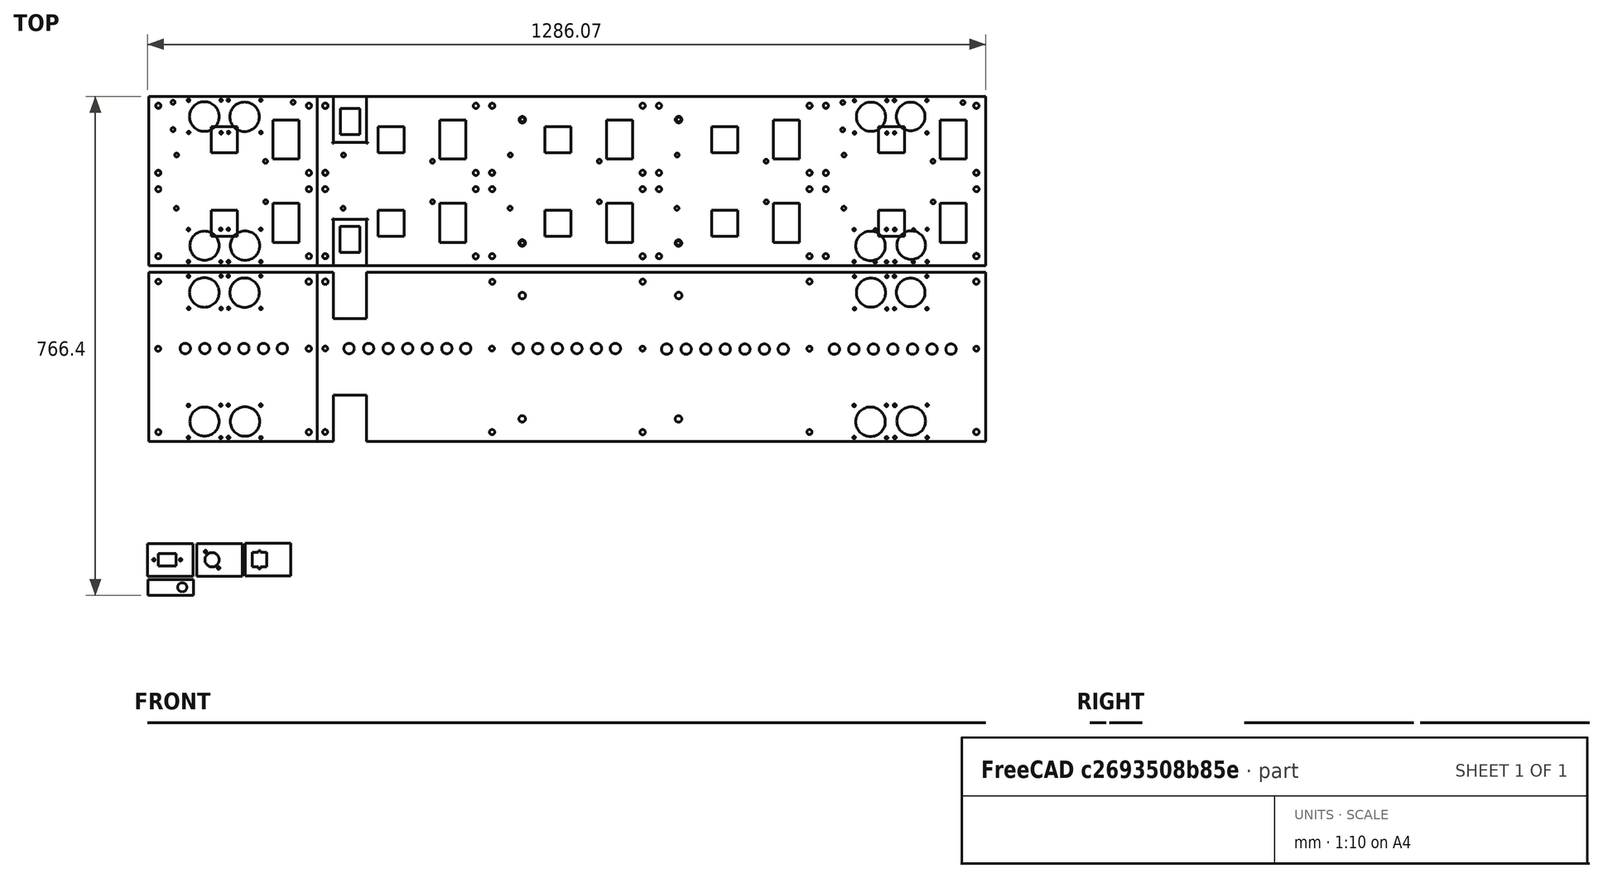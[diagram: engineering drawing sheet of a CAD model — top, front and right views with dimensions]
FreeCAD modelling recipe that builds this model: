
FCSTD DOCUMENT  (FreeCAD 1.0R39319 (Git))
Label: SurfSign-Case-4.2
License: All rights reserved
LicenseURL: https://en.wikipedia.org/wiki/All_rights_reserved
objects: Part::Part2DObjectPython×16, Part::FeaturePython×12, Part::Feature×4, Part::Cut×3, App::DocumentObjectGroup×2
note: 35 computed .brp shape members not serialized (recipe doc carries the construction recipe); baked Part::Feature solids carry a one-line shape summary decoded from their .brp

FEATURE [Part::Part2DObjectPython] Rectangle024  label="SidesLarge"  # Draft 2D object (typed FeaturePython)
  Area = 55782
  ChamferSize = 0
  Columns = 1
  FilletRadius = 0
  Height = 54
  Length = 1033
  MakeFace = true
  Placement = pos=(95.949,-98.4324,0) rot=(0,0,1;0rad)
  Rows = 1
FEATURE [Part::Part2DObjectPython] Rectangle026  label="SidesSmall"  # Draft 2D object (typed FeaturePython)
  Area = 14040
  ChamferSize = 0
  Columns = 1
  FilletRadius = 0
  Height = 54
  Length = 260
  MakeFace = true
  Placement = pos=(93.675,-166.174,0) rot=(0,0,1;0rad)
  Rows = 1
FEATURE [Part::Part2DObjectPython] Rectangle027  # Draft 2D object (typed FeaturePython)
  Area = 1722
  ChamferSize = 0
  Columns = 1
  FilletRadius = 0
  Height = 24.6
  Length = 70
  MakeFace = true
  Placement = pos=(121.424,-273.33,0) rot=(0,0,1;0rad)
  Rows = 1
FEATURE [Part::Part2DObjectPython] Circle024  # Draft 2D object (typed FeaturePython)
  Area = 153.938
  FirstAngle = 0
  LastAngle = 0
  MakeFace = true
  Placement = pos=(173.98,-260.68,0) rot=(0,0,1;0rad)
  Radius = 7
FEATURE [Part::Cut] Cut017  label="PeriphrealSides"
  Base = -> Rectangle027
  Placement = pos=(-22.8217,16.9303,0) rot=(0,0,1;0rad)
  Refine = true
  Tool = -> Circle024
FEATURE [Part::Feature] Subtraction032  label="PeriphrealPower"
  Placement = pos=(-0.595688,35.1452,0) rot=(0,0,1;0rad)
  shape: bbox 70 x 50 x 2e-07 mm, 1 faces, 0 solids (baked)
FEATURE [Part::Part2DObjectPython] Rectangle029  # Draft 2D object (typed FeaturePython)
  Area = 484
  ChamferSize = 0
  Columns = 1
  FilletRadius = 0
  Height = 22
  Length = 22
  MakeFace = true
  Placement = pos=(110.321,-299.863,0) rot=(0,0,1;0rad)
  Rows = 1
FEATURE [Part::Part2DObjectPython] Rectangle028  # Draft 2D object (typed FeaturePython)
  Area = 3500
  ChamferSize = 0
  Columns = 1
  FilletRadius = 0
  Height = 50
  Length = 70
  MakeFace = true
  Placement = pos=(99.2536,-313.899,0) rot=(0,0,1;0rad)
  Rows = 1
FEATURE [Part::Cut] Cut018
  Base = -> Rectangle028
  Refine = true
  Tool = -> Rectangle029
FEATURE [Part::Part2DObjectPython] Rectangle031  # Draft 2D object (typed FeaturePython)
  Area = 84
  ChamferSize = 0
  Columns = 1
  FilletRadius = 0
  Height = 28
  Length = 3
  MakeFace = true
  Placement = pos=(119.9,-302.833,0) rot=(0,0,1;0rad)
  Rows = 1
FEATURE [Part::Cut] Cut019  label="PeriphrealRJ45A"
  Base = -> Cut018
  Placement = pos=(148.325,87.5652,0) rot=(0,0,1;0rad)
  Refine = true
  Tool = -> Rectangle031
FEATURE [Part::Feature] Subtraction033  label="PeriphrealRJ45B"
  Placement = pos=(73.2688,140.581,0) rot=(0,0,1;0rad)
  shape: bbox 70 x 50 x 2e-07 mm, 1 faces, 0 solids (baked)
FEATURE [Part::FeaturePython] Clone  label="Backplate"  # WARN: FeaturePython — macro-defined, semantics opaque (R4)
  AttacherType = Attacher::AttachEngine3D
  Fuse = false
  Placement = pos=(2.11317,-14.857,0) rot=(0,0,1;0rad)
  Scale = (1,1,1)
FEATURE [Part::Part2DObjectPython] Rectangle032  label="SidesLarge001"  # Draft 2D object (typed FeaturePython)
  Area = 55782
  ChamferSize = 0
  Columns = 1
  FilletRadius = 0
  Height = 54
  Length = 1033
  MakeFace = true
  Placement = pos=(95.949,-98.4324,0) rot=(0,0,1;0rad)
  Rows = 1
FEATURE [Part::Feature] Subtraction
  shape: bbox 1284 x 260 x 2e-07 mm, 1 faces, 0 solids (baked)
FEATURE [Part::Part2DObjectPython] Line  # Draft 2D object (typed FeaturePython)
  Area = 0
  ChamferSize = 0
  Closed = false
  End = (358,558.007,0)
  FilletRadius = 0
  Length = 578.437
  MakeFace = true
  Placement = pos=(358,-20.4298,0) rot=(0,0,1;0rad)
  Points = (2) [(0,0,0),(0,578.437,0)]
  Start = (358,-20.4298,0)
  Subdivisions = 0
FEATURE [Part::Part2DObjectPython] Rectangle  # Draft 2D object (typed FeaturePython)
  Area = 8149.48
  ChamferSize = 0
  Columns = 1
  FilletRadius = 0
  Height = 42.278
  Length = 192.759
  MakeFace = true
  Placement = pos=(146.23,98.5195,0) rot=(0,0,1;0rad)
  Rows = 1
FEATURE [Part::Part2DObjectPython] Rectangle033  # Draft 2D object (typed FeaturePython)
  Area = 12120.2
  ChamferSize = 0
  Columns = 1
  FilletRadius = 0
  Height = 60.1925
  Length = 201.358
  MakeFace = true
  Placement = pos=(400.615,90.6372,0) rot=(0,0,1;0rad)
  Rows = 1
FEATURE [Part::Part2DObjectPython] Rectangle034  # Draft 2D object (typed FeaturePython)
  Area = 11122.6
  ChamferSize = 0
  Columns = 1
  FilletRadius = 0
  Height = 55.8061
  Length = 199.308
  MakeFace = true
  Placement = pos=(646.161,92.4922,0) rot=(0,0,1;0rad)
  Rows = 1
FEATURE [Part::Part2DObjectPython] Rectangle035  # Draft 2D object (typed FeaturePython)
  Area = 12467.7
  ChamferSize = 0
  Columns = 1
  FilletRadius = 0
  Height = 61.5007
  Length = 202.724
  MakeFace = true
  Placement = pos=(885.33,90.2144,0) rot=(0,0,1;0rad)
  Rows = 1
FEATURE [Part::Part2DObjectPython] Rectangle036  # Draft 2D object (typed FeaturePython)
  Area = 11544.2
  ChamferSize = 0
  Columns = 1
  FilletRadius = 0
  Height = 56.9451
  Length = 202.724
  MakeFace = true
  Placement = pos=(1154.11,90.2144,0) rot=(0,0,1;0rad)
  Rows = 1
FEATURE [Part::FeaturePython] Embed  # WARN: FeaturePython — macro-defined, semantics opaque (R4)
  Base = -> Subtraction
  Refine = true
  Tolerance = 0
  Tool = -> Rectangle
FEATURE [Part::FeaturePython] Embed001  # WARN: FeaturePython — macro-defined, semantics opaque (R4)
  Base = -> Embed
  Refine = true
  Tolerance = 0
  Tool = -> Rectangle036
FEATURE [Part::FeaturePython] Embed002  # WARN: FeaturePython — macro-defined, semantics opaque (R4)
  Base = -> Embed001
  Refine = true
  Tolerance = 0
  Tool = -> Rectangle035
FEATURE [Part::FeaturePython] Embed003  # WARN: FeaturePython — macro-defined, semantics opaque (R4)
  Base = -> Embed002
  Refine = true
  Tolerance = 0
  Tool = -> Rectangle034
FEATURE [Part::FeaturePython] Embed004  # WARN: FeaturePython — macro-defined, semantics opaque (R4)
  Base = -> Embed003
  Placement = pos=(-7.62939e-06,270,0) rot=(0,0,1;0rad)
  Refine = true
  Tolerance = 0
  Tool = -> Rectangle033
FEATURE [Part::Part2DObjectPython] Rectangle037  # Draft 2D object (typed FeaturePython)
  Area = 5623.78
  ChamferSize = 0
  Columns = 1
  FilletRadius = 0
  Height = 249.812
  Length = 22.5121
  MakeFace = true
  Placement = pos=(1129.73,252.982,0) rot=(0,0,1;0rad)
  Rows = 1
FEATURE [Part::Feature] Subtraction035
  shape: bbox 1284 x 260 x 2e-07 mm, 1 faces, 0 solids (baked)
FEATURE [Part::Part2DObjectPython] Line001  # Draft 2D object (typed FeaturePython)
  Area = 0
  ChamferSize = 0
  Closed = false
  End = (358,558.007,0)
  FilletRadius = 0
  Length = 578.437
  MakeFace = true
  Placement = pos=(358,-20.4298,0) rot=(0,0,1;0rad)
  Points = (2) [(0,0,0),(0,578.437,0)]
  Start = (358,-20.4298,0)
  Subdivisions = 0
FEATURE [Part::FeaturePython] Slice  # WARN: FeaturePython — macro-defined, semantics opaque (R4)
  Base = -> Subtraction035
  Mode = 1
  Tolerance = 0
  Tools = -> [Line]
FEATURE [Part::FeaturePython] Slice_child0  label="Slice.0"  # WARN: FeaturePython — macro-defined, semantics opaque (R4)
  Base = -> Slice
  FilterType = 1
  Invert = false
  OverrideMaxVal = 0
  WindowFrom = 80
  WindowTo = 100
  items = 0
FEATURE [Part::FeaturePython] Slice_child1  label="Slice.1"  # WARN: FeaturePython — macro-defined, semantics opaque (R4)
  Base = -> Slice
  FilterType = 1
  Invert = false
  OverrideMaxVal = 0
  WindowFrom = 80
  WindowTo = 100
  items = 1
FEATURE [App::DocumentObjectGroup] GrExplode_Slice  label="Exploded Slice"
  Group = -> [Slice_child0,Slice_child1]
FEATURE [Part::FeaturePython] Slice001  # WARN: FeaturePython — macro-defined, semantics opaque (R4)
  Base = -> Clone
  Mode = 1
  Tolerance = 0
  Tools = -> [Line001]
FEATURE [Part::FeaturePython] Slice001_child0  label="Slice001.0"  # WARN: FeaturePython — macro-defined, semantics opaque (R4)
  Base = -> Slice001
  FilterType = 1
  Invert = false
  OverrideMaxVal = 0
  WindowFrom = 80
  WindowTo = 100
  items = 0
FEATURE [Part::FeaturePython] Slice001_child1  label="Slice001.1"  # WARN: FeaturePython — macro-defined, semantics opaque (R4)
  Base = -> Slice001
  FilterType = 1
  Invert = false
  OverrideMaxVal = 0
  WindowFrom = 80
  WindowTo = 100
  items = 1
FEATURE [App::DocumentObjectGroup] GrExplode_Slice001  label="Exploded Slice001"
  Group = -> [Slice001_child0,Slice001_child1]
